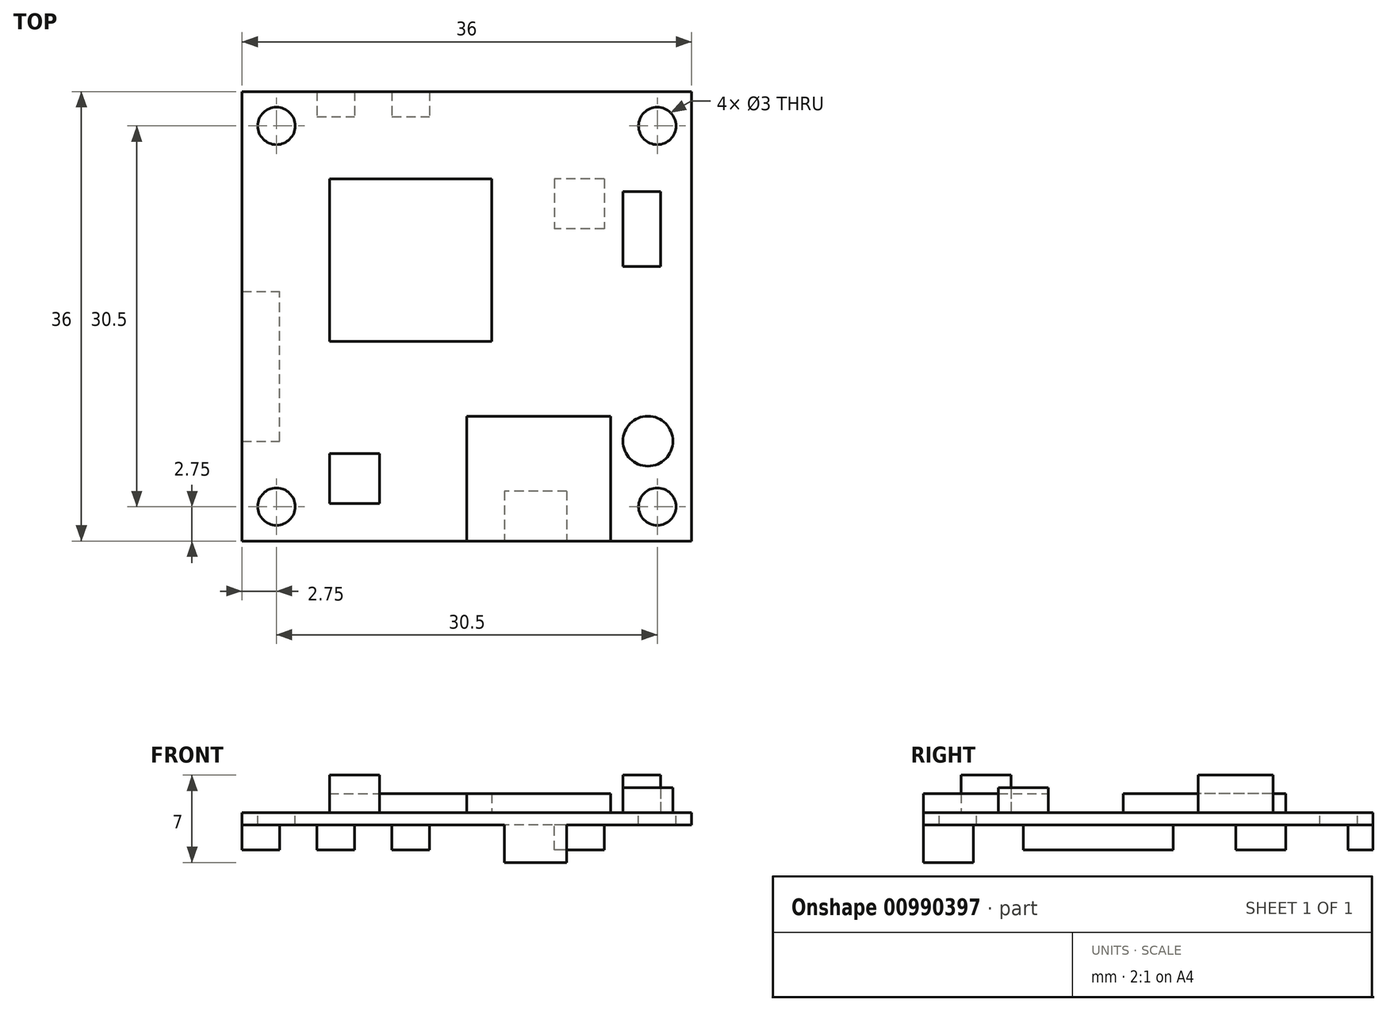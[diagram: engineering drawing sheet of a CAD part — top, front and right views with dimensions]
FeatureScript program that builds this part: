
annotation { "Feature Type Name" : "Feature", "Feature Type Description" : "" }
export const myFeature = defineFeature(function(context is Context, id is Id, definition is map)
    precondition{}
    {
        {
            var Q0;
            Q0=qCreatedBy(makeId("Top.planeOp"),FACE);
            var sketch = newSketch(context, id + "F0", { "sketchPlane" : qUnion([Q0])});
            skCircle(sketch, "E0", {"center": v(-15.25, 15.25) * mm, "radius": 1.5 * mm});
            skCircle(sketch, "E1.0.1.0", {"center": v(-15.25, -15.25) * mm, "radius": 1.5 * mm});
            skCircle(sketch, "E1.1.0.0", {"center": v(15.25, 15.25) * mm, "radius": 1.5 * mm});
            skCircle(sketch, "E1.1.1.0", {"center": v(15.25, -15.25) * mm, "radius": 1.5 * mm});
            skLineSegment(sketch, "E1.direction1", {"start": v(-15.25, 15.25) * mm, "end": v(15.25, 15.25) * mm, "construction": true});
            skLineSegment(sketch, "E1.direction2", {"start": v(-15.25, 15.25) * mm, "end": v(-15.25, -15.25) * mm, "construction": true});
            skLineSegment(sketch, "E2.bottom", {"start": v(-18, -18) * mm, "end": v(18, -18) * mm});
            skLineSegment(sketch, "E2.top", {"start": v(-18, 18) * mm, "end": v(18, 18) * mm});
            skLineSegment(sketch, "E2.left", {"start": v(-18, -18) * mm, "end": v(-18, 18) * mm});
            skLineSegment(sketch, "E2.right", {"start": v(18, -18) * mm, "end": v(18, 18) * mm});
            skPoint(sketch, "E2.middle", {"position": v(0, 0) * mm});
            skSolve(sketch);
        }
        {
            var Q0;
            Q0=makeQuery(id+"F0.imprint","IMPRINT",FACE,{"disambiguationData":[TD([[makeQuery(id+"F0.imprint","IMPRINT",EDGE,{"derivedFrom":sQuery(id+"F0.wireOp",EDGE,"E0")}),-1.0]])]});
            var sketch = newSketch(context, id + "F1", { "sketchPlane" : qUnion([Q0])});
            skLineSegment(sketch, "E3.bottom", {"start": v(-11, 11) * mm, "end": v(2, 11) * mm});
            skLineSegment(sketch, "E3.top", {"start": v(-11, -2) * mm, "end": v(2, -2) * mm});
            skLineSegment(sketch, "E3.left", {"start": v(-11, 11) * mm, "end": v(-11, -2) * mm});
            skLineSegment(sketch, "E3.right", {"start": v(2, 11) * mm, "end": v(2, -2) * mm});
            skLineSegment(sketch, "E4.bottom", {"start": v(11.5, -18) * mm, "end": v(0, -18) * mm});
            skLineSegment(sketch, "E4.top", {"start": v(11.5, -8) * mm, "end": v(0, -8) * mm});
            skLineSegment(sketch, "E4.left", {"start": v(11.5, -18) * mm, "end": v(11.5, -8) * mm});
            skLineSegment(sketch, "E4.right", {"start": v(0, -18) * mm, "end": v(0, -8) * mm});
            skLineSegment(sketch, "E5.bottom", {"start": v(15.5, 10) * mm, "end": v(12.5, 10) * mm});
            skLineSegment(sketch, "E5.top", {"start": v(15.5, 4) * mm, "end": v(12.5, 4) * mm});
            skLineSegment(sketch, "E5.left", {"start": v(15.5, 10) * mm, "end": v(15.5, 4) * mm});
            skLineSegment(sketch, "E5.right", {"start": v(12.5, 10) * mm, "end": v(12.5, 4) * mm});
            skLineSegment(sketch, "E6.bottom", {"start": v(-7, -15) * mm, "end": v(-11, -15) * mm});
            skLineSegment(sketch, "E6.top", {"start": v(-7, -11) * mm, "end": v(-11, -11) * mm});
            skLineSegment(sketch, "E6.left", {"start": v(-7, -15) * mm, "end": v(-7, -11) * mm});
            skLineSegment(sketch, "E6.right", {"start": v(-11, -15) * mm, "end": v(-11, -11) * mm});
            skCircle(sketch, "E7", {"center": v(14.5, -10) * mm, "radius": 2 * mm});
            skSolve(sketch);
        }
        {
            var Q0;
            Q0=makeQuery(id+"F1.imprint","IMPRINT",FACE,{"disambiguationData":[TD([[makeQuery(id+"F1.imprint","IMPRINT",EDGE,{"derivedFrom":sQuery(id+"F1.wireOp",EDGE,"E3.bottom")}),-1.0]])]});
            var Q1;
            Q1=makeQuery(id+"F1.imprint","IMPRINT",FACE,{"disambiguationData":[TD([[makeQuery(id+"F1.imprint","IMPRINT",EDGE,{"derivedFrom":sQuery(id+"F1.wireOp",EDGE,"E4.bottom")}),1.0]])]});
            extrude(context, id + "F2", {"entities" : qUnion([Q0, Q1]), "depth" : 1.5 * mm, "offsetDistance" : 25 * mm});
        }
        {
            var Q0;
            Q0=makeQuery(id+"F1.imprint","IMPRINT",FACE,{"disambiguationData":[TD([[makeQuery(id+"F1.imprint","IMPRINT",EDGE,{"derivedFrom":sQuery(id+"F1.wireOp",EDGE,"E7")}),1.0]])]});
            extrude(context, id + "F3", {"entities" : qUnion([Q0]), "depth" : 2 * mm, "offsetDistance" : 25 * mm});
        }
        {
            var Q0;
            Q0=makeQuery(id+"F1.imprint","IMPRINT",FACE,{"disambiguationData":[TD([[makeQuery(id+"F1.imprint","IMPRINT",EDGE,{"derivedFrom":sQuery(id+"F1.wireOp",EDGE,"E5.bottom")}),1.0]])]});
            var Q1;
            Q1=makeQuery(id+"F1.imprint","IMPRINT",FACE,{"disambiguationData":[TD([[makeQuery(id+"F1.imprint","IMPRINT",EDGE,{"derivedFrom":sQuery(id+"F1.wireOp",EDGE,"E6.bottom")}),-1.0]])]});
            extrude(context, id + "F4", {"entities" : qUnion([Q0, Q1]), "depth" : 3 * mm, "offsetDistance" : 25 * mm});
        }
        {
            var Q0;
            Q0 = qSketchRegion(id + "F0", true);
            extrude(context, id + "F5", {"entities" : qUnion([Q0]), "oppositeDirection" : true, "depth" : 1 * mm, "offsetDistance" : 25 * mm});
        }
        {
            var Q0;
            Q0=makeQuery(id+"F5.opExtrude","CAP_FACE",FACE,{"disambiguationData":[OSD([sQuery(id+"F0.wireOp",EDGE,"E0"),sQuery(id+"F0.wireOp",EDGE,"E1.0.1.0"),sQuery(id+"F0.wireOp",EDGE,"E1.1.0.0"),sQuery(id+"F0.wireOp",EDGE,"E1.1.1.0"),sQuery(id+"F0.wireOp",EDGE,"E2.bottom"),sQuery(id+"F0.wireOp",EDGE,"E2.top"),sQuery(id+"F0.wireOp",EDGE,"E2.left"),sQuery(id+"F0.wireOp",EDGE,"E2.right")])],"isStart":false});
            var sketch = newSketch(context, id + "F6", { "sketchPlane" : qUnion([Q0])});
            skLineSegment(sketch, "E8.bottom", {"start": v(8, 14) * mm, "end": v(3, 14) * mm});
            skLineSegment(sketch, "E8.top", {"start": v(8, 18) * mm, "end": v(3, 18) * mm});
            skLineSegment(sketch, "E8.left", {"start": v(8, 14) * mm, "end": v(8, 18) * mm});
            skLineSegment(sketch, "E8.right", {"start": v(3, 14) * mm, "end": v(3, 18) * mm});
            skLineSegment(sketch, "E9.bottom", {"start": v(-18, 10) * mm, "end": v(-15, 10) * mm});
            skLineSegment(sketch, "E9.top", {"start": v(-18, -2) * mm, "end": v(-15, -2) * mm});
            skLineSegment(sketch, "E9.left", {"start": v(-18, 10) * mm, "end": v(-18, -2) * mm});
            skLineSegment(sketch, "E9.right", {"start": v(-15, 10) * mm, "end": v(-15, -2) * mm});
            skLineSegment(sketch, "E10.bottom", {"start": v(-12, -18) * mm, "end": v(-9, -18) * mm});
            skLineSegment(sketch, "E10.top", {"start": v(-12, -16) * mm, "end": v(-9, -16) * mm});
            skLineSegment(sketch, "E10.left", {"start": v(-12, -18) * mm, "end": v(-12, -16) * mm});
            skLineSegment(sketch, "E10.right", {"start": v(-9, -18) * mm, "end": v(-9, -16) * mm});
            skLineSegment(sketch, "E11.bottom", {"start": v(-6, -18) * mm, "end": v(-3, -18) * mm});
            skLineSegment(sketch, "E11.top", {"start": v(-6, -16) * mm, "end": v(-3, -16) * mm});
            skLineSegment(sketch, "E11.left", {"start": v(-6, -18) * mm, "end": v(-6, -16) * mm});
            skLineSegment(sketch, "E11.right", {"start": v(-3, -18) * mm, "end": v(-3, -16) * mm});
            skLineSegment(sketch, "E12.bottom", {"start": v(11, -11) * mm, "end": v(7, -11) * mm});
            skLineSegment(sketch, "E12.top", {"start": v(11, -7) * mm, "end": v(7, -7) * mm});
            skLineSegment(sketch, "E12.left", {"start": v(11, -11) * mm, "end": v(11, -7) * mm});
            skLineSegment(sketch, "E12.right", {"start": v(7, -11) * mm, "end": v(7, -7) * mm});
            skSolve(sketch);
        }
        {
            var Q0;
            Q0=makeQuery(id+"F6.imprint","IMPRINT",FACE,{"disambiguationData":[TD([[makeQuery(id+"F6.imprint","IMPRINT",EDGE,{"derivedFrom":sQuery(id+"F6.wireOp",EDGE,"E11.bottom")}),1.0]])]});
            var Q1;
            Q1=makeQuery(id+"F6.imprint","IMPRINT",FACE,{"disambiguationData":[TD([[makeQuery(id+"F6.imprint","IMPRINT",EDGE,{"derivedFrom":sQuery(id+"F6.wireOp",EDGE,"E10.bottom")}),1.0]])]});
            var Q2;
            Q2=makeQuery(id+"F6.imprint","IMPRINT",FACE,{"disambiguationData":[TD([[makeQuery(id+"F6.imprint","IMPRINT",EDGE,{"derivedFrom":sQuery(id+"F6.wireOp",EDGE,"E12.bottom")}),-1.0]])]});
            var Q3;
            Q3=makeQuery(id+"F6.imprint","IMPRINT",FACE,{"disambiguationData":[TD([[makeQuery(id+"F6.imprint","IMPRINT",EDGE,{"derivedFrom":sQuery(id+"F6.wireOp",EDGE,"E9.bottom")}),-1.0]])]});
            extrude(context, id + "F7", {"entities" : qUnion([Q0, Q1, Q2, Q3]), "depth" : 2 * mm, "offsetDistance" : 25 * mm});
        }
        {
            var Q0;
            Q0=makeQuery(id+"F6.imprint","IMPRINT",FACE,{"disambiguationData":[TD([[makeQuery(id+"F6.imprint","IMPRINT",EDGE,{"derivedFrom":sQuery(id+"F6.wireOp",EDGE,"E8.bottom")}),-1.0]])]});
            extrude(context, id + "F8", {"entities" : qUnion([Q0]), "operationType" : NewBodyOperationType.ADD, "depth" : 3 * mm, "offsetDistance" : 25 * mm});
        }
    });
